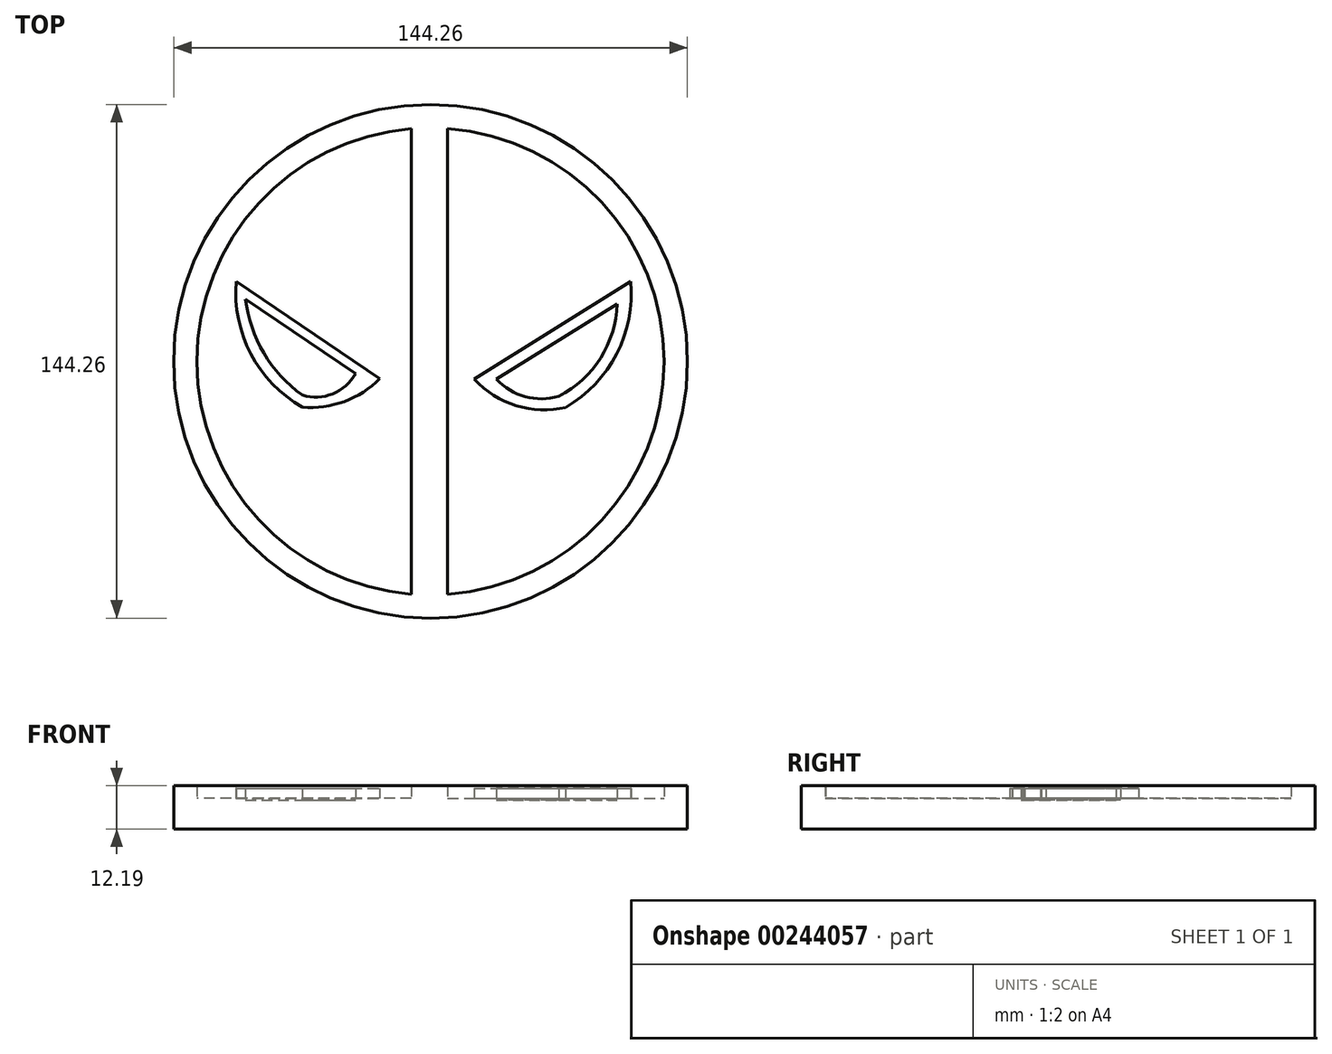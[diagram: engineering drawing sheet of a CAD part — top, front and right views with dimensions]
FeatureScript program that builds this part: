
annotation { "Feature Type Name" : "Feature", "Feature Type Description" : "" }
export const myFeature = defineFeature(function(context is Context, id is Id, definition is map)
    precondition{}
    {
        {
            var Q0;
            Q0=qCreatedBy(makeId("Top.planeOp"),FACE);
            var sketch = newSketch(context, id + "F0", { "sketchPlane" : qUnion([Q0])});
            skCircle(sketch, "E0", {"center": v(0, 0) * mm, "radius": 72.13 * mm});
            skCircle(sketch, "E1", {"center": v(0, 0) * mm, "radius": 65.58 * mm});
            skLineSegment(sketch, "E2", {"start": v(-5.4, 65.36) * mm, "end": v(-5.4, -65.36) * mm});
            skLineSegment(sketch, "E3", {"start": v(4.8, 65.4) * mm, "end": v(4.8, -65.4) * mm});
            skLineSegment(sketch, "E4", {"start": v(-61.6, 22.51) * mm, "end": v(61.6, 22.51) * mm, "construction": true});
            skLineSegment(sketch, "E5", {"start": v(-64.31, -12.84) * mm, "end": v(64.31, -12.84) * mm, "construction": true});
            skLineSegment(sketch, "E6", {"start": v(-54.57, 22.51) * mm, "end": v(-14.26, -4.81) * mm});
            skArc(sketch, "E7", {"start": v(-36, -12.84) * mm, "mid": v(-24.23, -11.26) * mm, "end": v(-14.26, -4.81) * mm});
            skArc(sketch, "E8", {"start": v(-54.57, 22.51) * mm, "mid": v(-50.44, 2.13) * mm, "end": v(-36, -12.84) * mm});
            skLineSegment(sketch, "E9", {"start": v(12.26, -5.03) * mm, "end": v(56.2, 22.51) * mm});
            skArc(sketch, "E10", {"start": v(12.26, -5.03) * mm, "mid": v(24.06, -12.4) * mm, "end": v(37.97, -12.95) * mm});
            skArc(sketch, "E11", {"start": v(37.97, -12.95) * mm, "mid": v(52.24, 2.13) * mm, "end": v(56.2, 22.51) * mm});
            skLineSegment(sketch, "E12", {"start": v(-51.98, 17.52) * mm, "end": v(-21.07, -3.43) * mm});
            skArc(sketch, "E13", {"start": v(-51.98, 17.52) * mm, "mid": v(-46.8, 2.35) * mm, "end": v(-36, -9.47) * mm});
            skArc(sketch, "E14", {"start": v(-36, -9.47) * mm, "mid": v(-27.46, -9.1) * mm, "end": v(-21.07, -3.43) * mm});
            skLineSegment(sketch, "E15", {"start": v(52.32, 16.18) * mm, "end": v(18.52, -5) * mm});
            skArc(sketch, "E16", {"start": v(18.52, -5) * mm, "mid": v(26.57, -9.9) * mm, "end": v(36, -9.76) * mm});
            skArc(sketch, "E17", {"start": v(36, -9.76) * mm, "mid": v(47.75, 0.94) * mm, "end": v(52.32, 16.18) * mm});
            skSolve(sketch);
        }
        {
            var Q0;
            Q0=makeQuery(id+"F0.imprint","IMPRINT",FACE,{"disambiguationData":[TD([[makeQuery(id+"F0.imprint","IMPRINT",EDGE,{"derivedFrom":sQuery(id+"F0.wireOp",EDGE,"E0")}),1.0]])]});
            var Q1;
            {var subQ0=sQuery(id+"F0.wireOp",EDGE,"E2");Q1=makeQuery(id+"F0.imprint","IMPRINT",FACE,{"disambiguationData":[TD([[makeQuery(id+"F0.imprint","IMPRINT",EDGE,{"derivedFrom":subQ0}),1.0]])]});}
            extrude(context, id + "F1", {"entities" : qUnion([Q0, Q1]), "depth" : 12.2 * mm});
        }
        {
            var Q0;
            {var subQ0=sQuery(id+"F0.wireOp",EDGE,"E2");Q0=makeQuery(id+"F0.imprint","IMPRINT",FACE,{"disambiguationData":[TD([[makeQuery(id+"F0.imprint","IMPRINT",EDGE,{"derivedFrom":subQ0}),-1.0]])]});}
            var Q1;
            {var subQ0=sQuery(id+"F0.wireOp",EDGE,"E3");Q1=makeQuery(id+"F0.imprint","IMPRINT",FACE,{"disambiguationData":[TD([[makeQuery(id+"F0.imprint","IMPRINT",EDGE,{"derivedFrom":subQ0}),1.0]])]});}
            extrude(context, id + "F2", {"entities" : qUnion([Q0, Q1]), "operationType" : NewBodyOperationType.ADD, "depth" : 8.64 * mm});
        }
        {
            var Q0;
            Q0=makeQuery(id+"F0.imprint","IMPRINT",FACE,{"disambiguationData":[TD([[makeQuery(id+"F0.imprint","IMPRINT",EDGE,{"derivedFrom":sQuery(id+"F0.wireOp",EDGE,"E6")}),-1.0]])]});
            var Q1;
            Q1=makeQuery(id+"F0.imprint","IMPRINT",FACE,{"disambiguationData":[TD([[makeQuery(id+"F0.imprint","IMPRINT",EDGE,{"derivedFrom":sQuery(id+"F0.wireOp",EDGE,"E9")}),-1.0]])]});
            extrude(context, id + "F3", {"entities" : qUnion([Q0, Q1]), "operationType" : NewBodyOperationType.ADD, "depth" : 11.43 * mm});
        }
        {
            var Q0;
            Q0=makeQuery(id+"F0.imprint","IMPRINT",FACE,{"disambiguationData":[TD([[makeQuery(id+"F0.imprint","IMPRINT",EDGE,{"derivedFrom":sQuery(id+"F0.wireOp",EDGE,"E12")}),-1.0]])]});
            var Q1;
            Q1=makeQuery(id+"F0.imprint","IMPRINT",FACE,{"disambiguationData":[TD([[makeQuery(id+"F0.imprint","IMPRINT",EDGE,{"derivedFrom":sQuery(id+"F0.wireOp",EDGE,"E15")}),1.0]])]});
            extrude(context, id + "F4", {"entities" : qUnion([Q0, Q1]), "operationType" : NewBodyOperationType.ADD, "depth" : 8.13 * mm});
        }
    });
